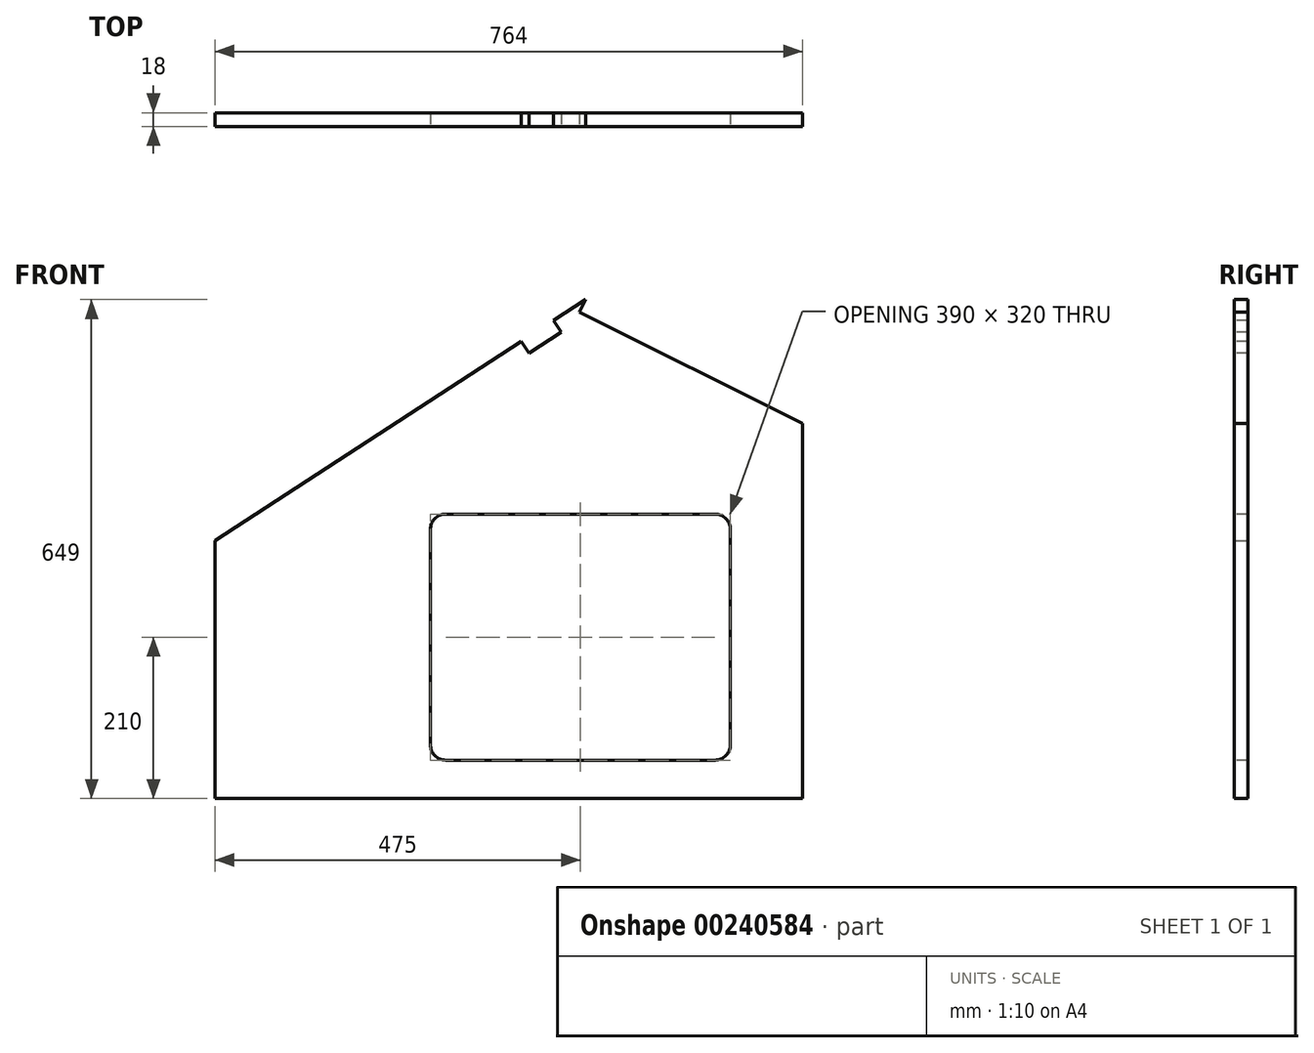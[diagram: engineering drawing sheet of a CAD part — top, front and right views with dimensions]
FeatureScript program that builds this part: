
annotation { "Feature Type Name" : "Feature", "Feature Type Description" : "" }
export const myFeature = defineFeature(function(context is Context, id is Id, definition is map)
    precondition{}
    {
        {
            var Q0;
            Q0=qCreatedBy(makeId("Front.planeOp"),FACE);
            var sketch = newSketch(context, id + "F0", { "sketchPlane" : qUnion([Q0])});
            skLineSegment(sketch, "E0.bottom", {"start": v(0, 0) * mm, "end": v(800, 0) * mm, "construction": true});
            skLineSegment(sketch, "E0.top", {"start": v(0, 1000) * mm, "end": v(800, 1000) * mm, "construction": true});
            skLineSegment(sketch, "E0.left", {"start": v(0, 0) * mm, "end": v(0, 1000) * mm, "construction": true});
            skLineSegment(sketch, "E0.right", {"start": v(800, 0) * mm, "end": v(800, 1000) * mm, "construction": true});
            skLineSegment(sketch, "E1.bottom", {"start": v(100, 0) * mm, "end": v(700, 0) * mm, "construction": true});
            skLineSegment(sketch, "E1.top", {"start": v(150, 325) * mm, "end": v(650, 325) * mm, "construction": true});
            skLineSegment(sketch, "E1.left", {"start": v(100, 0) * mm, "end": v(100, 275) * mm, "construction": true});
            skLineSegment(sketch, "E1.right", {"start": v(700, 0) * mm, "end": v(700, 275) * mm, "construction": true});
            skLineSegment(sketch, "E2", {"start": v(0, 675) * mm, "end": v(500, 1000) * mm, "construction": true});
            skLineSegment(sketch, "E3", {"start": v(500, 1000) * mm, "end": v(800, 850) * mm, "construction": true});
            skPoint(sketch, "E4.visualSharp", {"position": v(100, 325) * mm});
            skArc(sketch, "E4.filletArc", {"start": v(150, 325) * mm, "mid": v(114.64, 310.36) * mm, "end": v(100, 275) * mm, "construction": true});
            skPoint(sketch, "E5.visualSharp", {"position": v(700, 325) * mm});
            skArc(sketch, "E5.filletArc", {"start": v(700, 275) * mm, "mid": v(685.36, 310.36) * mm, "end": v(650, 325) * mm, "construction": true});
            skLineSegment(sketch, "E6", {"start": v(18, 686.7) * mm, "end": v(18, 351) * mm});
            skLineSegment(sketch, "E7", {"start": v(18, 351) * mm, "end": v(782, 351) * mm});
            skLineSegment(sketch, "E8", {"start": v(782, 351) * mm, "end": v(782, 859) * mm});
            skLineSegment(sketch, "E9", {"start": v(782, 859) * mm, "end": v(500, 1000) * mm});
            skLineSegment(sketch, "E10", {"start": v(500, 1000) * mm, "end": v(18, 686.7) * mm});
            skSolve(sketch);
        }
        {
            var Q0;
            Q0=makeQuery(id+"F0.imprint","IMPRINT",FACE,{"disambiguationData":[TD([[makeQuery(id+"F0.imprint","IMPRINT",EDGE,{"derivedFrom":sQuery(id+"F0.wireOp",EDGE,"E6")}),1.0]])]});
            extrude(context, id + "F1", {"entities" : qUnion([Q0]), "depth" : 18 * mm});
        }
        {
            var Q0;
            Q0=makeQuery(id+"F1.opExtrude","CAP_FACE",FACE,{"disambiguationData":[OSD([sQuery(id+"F0.wireOp",EDGE,"E6"),sQuery(id+"F0.wireOp",EDGE,"E7"),sQuery(id+"F0.wireOp",EDGE,"E8"),sQuery(id+"F0.wireOp",EDGE,"E9"),sQuery(id+"F0.wireOp",EDGE,"E10")])],"isStart":false});
            var sketch = newSketch(context, id + "F2", { "sketchPlane" : qUnion([Q0])});
            skLineSegment(sketch, "E11", {"start": v(125.77, 756.75) * mm, "end": v(119.23, 766.8) * mm, "construction": true});
            skLineSegment(sketch, "E12", {"start": v(119.23, 766.8) * mm, "end": v(161.15, 794.06) * mm, "construction": true});
            skLineSegment(sketch, "E13", {"start": v(161.15, 794.06) * mm, "end": v(167.69, 784) * mm, "construction": true});
            skLineSegment(sketch, "E14", {"start": v(167.69, 784) * mm, "end": v(125.77, 756.75) * mm, "construction": true});
            skLineSegment(sketch, "E15", {"start": v(332.31, 891) * mm, "end": v(325.77, 901.06) * mm, "construction": true});
            skLineSegment(sketch, "E16", {"start": v(325.77, 901.06) * mm, "end": v(367.7, 928.31) * mm, "construction": true});
            skLineSegment(sketch, "E17", {"start": v(367.7, 928.31) * mm, "end": v(374.23, 918.25) * mm, "construction": true});
            skLineSegment(sketch, "E18", {"start": v(374.23, 918.25) * mm, "end": v(332.31, 891) * mm, "construction": true});
            skLineSegment(sketch, "E19", {"start": v(18, 686.7) * mm, "end": v(0, 686.7) * mm, "construction": true});
            skLineSegment(sketch, "E20", {"start": v(0, 686.7) * mm, "end": v(0, 675) * mm, "construction": true});
            skLineSegment(sketch, "E21", {"start": v(0, 675) * mm, "end": v(18, 686.7) * mm, "construction": true});
            skSolve(sketch);
        }
        {
            var Q0;
            Q0=makeQuery(id+"F1.opExtrude","CAP_FACE",FACE,{"disambiguationData":[OSD([sQuery(id+"F0.wireOp",EDGE,"E6"),sQuery(id+"F0.wireOp",EDGE,"E7"),sQuery(id+"F0.wireOp",EDGE,"E8"),sQuery(id+"F0.wireOp",EDGE,"E9"),sQuery(id+"F0.wireOp",EDGE,"E10")])],"isStart":false});
            var sketch = newSketch(context, id + "F3", { "sketchPlane" : qUnion([Q0])});
            skLineSegment(sketch, "E22", {"start": v(607.33, 946.33) * mm, "end": v(612.7, 957.07) * mm, "construction": true});
            skLineSegment(sketch, "E23", {"start": v(567.98, 979.43) * mm, "end": v(612.7, 957.07) * mm, "construction": true});
            skLineSegment(sketch, "E24", {"start": v(567.98, 979.43) * mm, "end": v(562.6, 968.7) * mm, "construction": true});
            skLineSegment(sketch, "E25", {"start": v(607.33, 946.33) * mm, "end": v(562.6, 968.7) * mm, "construction": true});
            skLineSegment(sketch, "E26", {"start": v(692.67, 903.67) * mm, "end": v(698.04, 914.4) * mm, "construction": true});
            skLineSegment(sketch, "E27", {"start": v(698.04, 914.4) * mm, "end": v(742.76, 892.04) * mm, "construction": true});
            skLineSegment(sketch, "E28", {"start": v(742.76, 892.04) * mm, "end": v(737.4, 881.3) * mm, "construction": true});
            skLineSegment(sketch, "E29", {"start": v(737.4, 881.3) * mm, "end": v(692.67, 903.67) * mm, "construction": true});
            skLineSegment(sketch, "E30", {"start": v(782, 859) * mm, "end": v(800, 859) * mm, "construction": true});
            skLineSegment(sketch, "E31", {"start": v(800, 859) * mm, "end": v(800, 850) * mm, "construction": true});
            skLineSegment(sketch, "E32", {"start": v(800, 850) * mm, "end": v(782, 859) * mm, "construction": true});
            skSolve(sketch);
        }
        {
            var Q0;
            Q0=makeQuery(id+"FDaNYicRMPyxpko_1.boolean.opBoolean","MERGE",FACE,{"derivedFrom":[makeQuery(id+"F1.opExtrude","CAP_FACE",FACE,{"disambiguationData":[OSD([sQuery(id+"F0.wireOp",EDGE,"E6"),sQuery(id+"F0.wireOp",EDGE,"E7"),sQuery(id+"F0.wireOp",EDGE,"E8"),sQuery(id+"F0.wireOp",EDGE,"E9"),sQuery(id+"F0.wireOp",EDGE,"E10")])],"isStart":false}),makeQuery(id+"FDaNYicRMPyxpko_1.opExtrude","CAP_FACE",FACE,{"disambiguationData":[OSD([sQuery(id+"F2.wireOp",EDGE,"E11"),sQuery(id+"F2.wireOp",EDGE,"E12"),sQuery(id+"F2.wireOp",EDGE,"E13"),sQuery(id+"F2.wireOp",EDGE,"E14")])],"isStart":true}),makeQuery(id+"FDaNYicRMPyxpko_1.opExtrude","CAP_FACE",FACE,{"disambiguationData":[OSD([sQuery(id+"F2.wireOp",EDGE,"E15"),sQuery(id+"F2.wireOp",EDGE,"E16"),sQuery(id+"F2.wireOp",EDGE,"E17"),sQuery(id+"F2.wireOp",EDGE,"E18")])],"isStart":true}),makeQuery(id+"FDaNYicRMPyxpko_1.opExtrude","CAP_FACE",FACE,{"disambiguationData":[OSD([sQuery(id+"F3.wireOp",EDGE,"E22"),sQuery(id+"F3.wireOp",EDGE,"E23"),sQuery(id+"F3.wireOp",EDGE,"E24"),sQuery(id+"F3.wireOp",EDGE,"E25")])],"isStart":true}),makeQuery(id+"FDaNYicRMPyxpko_1.opExtrude","CAP_FACE",FACE,{"disambiguationData":[OSD([sQuery(id+"F3.wireOp",EDGE,"E26"),sQuery(id+"F3.wireOp",EDGE,"E27"),sQuery(id+"F3.wireOp",EDGE,"E28"),sQuery(id+"F3.wireOp",EDGE,"E29")])],"isStart":true})]});
            var sketch = newSketch(context, id + "F4", { "sketchPlane" : qUnion([Q0])});
            skLineSegment(sketch, "E33.bottom", {"start": v(298, 401) * mm, "end": v(688, 401) * mm});
            skLineSegment(sketch, "E33.top", {"start": v(298, 721) * mm, "end": v(688, 721) * mm});
            skLineSegment(sketch, "E33.left", {"start": v(298, 401) * mm, "end": v(298, 721) * mm});
            skLineSegment(sketch, "E33.right", {"start": v(688, 401) * mm, "end": v(688, 721) * mm});
            skSolve(sketch);
        }
        {
            var Q0;
            Q0 = qSketchRegion(id + "F4", true);
            extrude(context, id + "F5", {"entities" : qUnion([Q0]), "operationType" : NewBodyOperationType.REMOVE, "endBound" : BoundingType.UP_TO_NEXT, "oppositeDirection" : true, "depth" : 25 * mm, "offsetDistance" : 25 * mm});
        }
        {
            var Q0;
            Q0=makeQuery(id+"F5.boolean.opBoolean","COPY",EDGE,{"derivedFrom":makeQuery(id+"F5.opExtrude","SWEPT_EDGE",EDGE,{"disambiguationData":[OSD([sQuery(id+"F4.wireOp",EDGE,"E33.top"),sQuery(id+"F4.wireOp",EDGE,"E33.left")])]})});
            var Q1;
            Q1=makeQuery(id+"F5.boolean.opBoolean","COPY",EDGE,{"derivedFrom":makeQuery(id+"F5.opExtrude","SWEPT_EDGE",EDGE,{"disambiguationData":[OSD([sQuery(id+"F4.wireOp",EDGE,"E33.top"),sQuery(id+"F4.wireOp",EDGE,"E33.right")])]})});
            var Q2;
            Q2=makeQuery(id+"F5.boolean.opBoolean","COPY",EDGE,{"derivedFrom":makeQuery(id+"F5.opExtrude","SWEPT_EDGE",EDGE,{"disambiguationData":[OSD([sQuery(id+"F4.wireOp",EDGE,"E33.bottom"),sQuery(id+"F4.wireOp",EDGE,"E33.left")])]})});
            var Q3;
            Q3=makeQuery(id+"F5.boolean.opBoolean","COPY",EDGE,{"derivedFrom":makeQuery(id+"F5.opExtrude","SWEPT_EDGE",EDGE,{"disambiguationData":[OSD([sQuery(id+"F4.wireOp",EDGE,"E33.bottom"),sQuery(id+"F4.wireOp",EDGE,"E33.right")])]})});
            fillet(context, id + "F6", {"entities" : qUnion([Q0, Q1, Q2, Q3]), "radius" : 20 * mm, "tangentPropagation" : true, "allowEdgeOverflow" : false});
        }
        {
            var Q0;
            Q0=makeQuery(id+"F2.imprint","IMPRINT",FACE,{"disambiguationData":[TD([[makeQuery(id+"F2.imprint","IMPRINT",EDGE,{"derivedFrom":makeQuery(id+"F1.opExtrude","CAP_EDGE",EDGE,{"disambiguationData":[OSD([sQuery(id+"F0.wireOp",EDGE,"E6")])],"isStart":false})}),1.0]])]});
            var sketch = newSketch(context, id + "F7", { "sketchPlane" : qUnion([Q0])});
            skLineSegment(sketch, "E34", {"start": v(514.31, 972.72) * mm, "end": v(522.36, 988.82) * mm, "construction": true});
            skLineSegment(sketch, "E35", {"start": v(522.36, 988.82) * mm, "end": v(553.67, 973.17) * mm, "construction": true});
            skLineSegment(sketch, "E36", {"start": v(553.67, 973.17) * mm, "end": v(545.62, 957.07) * mm, "construction": true});
            skLineSegment(sketch, "E37", {"start": v(545.62, 957.07) * mm, "end": v(514.31, 972.72) * mm, "construction": true});
            skLineSegment(sketch, "E38", {"start": v(416.16, 945.5) * mm, "end": v(425.97, 930.4) * mm});
            skLineSegment(sketch, "E39", {"start": v(425.97, 930.4) * mm, "end": v(467.89, 957.66) * mm});
            skLineSegment(sketch, "E40", {"start": v(467.89, 957.66) * mm, "end": v(458.08, 972.75) * mm});
            skLineSegment(sketch, "E41", {"start": v(458.08, 972.75) * mm, "end": v(416.16, 945.5) * mm});
            skSolve(sketch);
        }
        {
            var Q0;
            Q0 = qSketchRegion(id + "F7", true);
            extrude(context, id + "F8", {"entities" : qUnion([Q0]), "operationType" : NewBodyOperationType.REMOVE, "oppositeDirection" : true, "depth" : 25 * mm, "offsetDistance" : 25 * mm});
        }
        {
            var Q0;
            Q0=makeQuery(id+"F2.imprint","IMPRINT",FACE,{"disambiguationData":[TD([[makeQuery(id+"F2.imprint","IMPRINT",EDGE,{"derivedFrom":makeQuery(id+"F1.opExtrude","CAP_EDGE",EDGE,{"disambiguationData":[OSD([sQuery(id+"F0.wireOp",EDGE,"E6")])],"isStart":false})}),1.0]])]});
            var sketch = newSketch(context, id + "F9", { "sketchPlane" : qUnion([Q0])});
            skLineSegment(sketch, "E42", {"start": v(500, 1000) * mm, "end": v(491.95, 983.9) * mm});
            skLineSegment(sketch, "E43", {"start": v(491.95, 983.9) * mm, "end": v(849.72, 805.01) * mm});
            skLineSegment(sketch, "E44", {"start": v(849.72, 805.01) * mm, "end": v(857.77, 821.11) * mm});
            skLineSegment(sketch, "E45", {"start": v(857.77, 821.11) * mm, "end": v(500, 1000) * mm});
            skSolve(sketch);
        }
        {
            var Q0;
            Q0 = qSketchRegion(id + "F9", true);
            extrude(context, id + "F10", {"entities" : qUnion([Q0]), "operationType" : NewBodyOperationType.REMOVE, "endBound" : BoundingType.UP_TO_NEXT, "oppositeDirection" : true, "depth" : 25 * mm, "offsetDistance" : 25 * mm});
        }
    });
